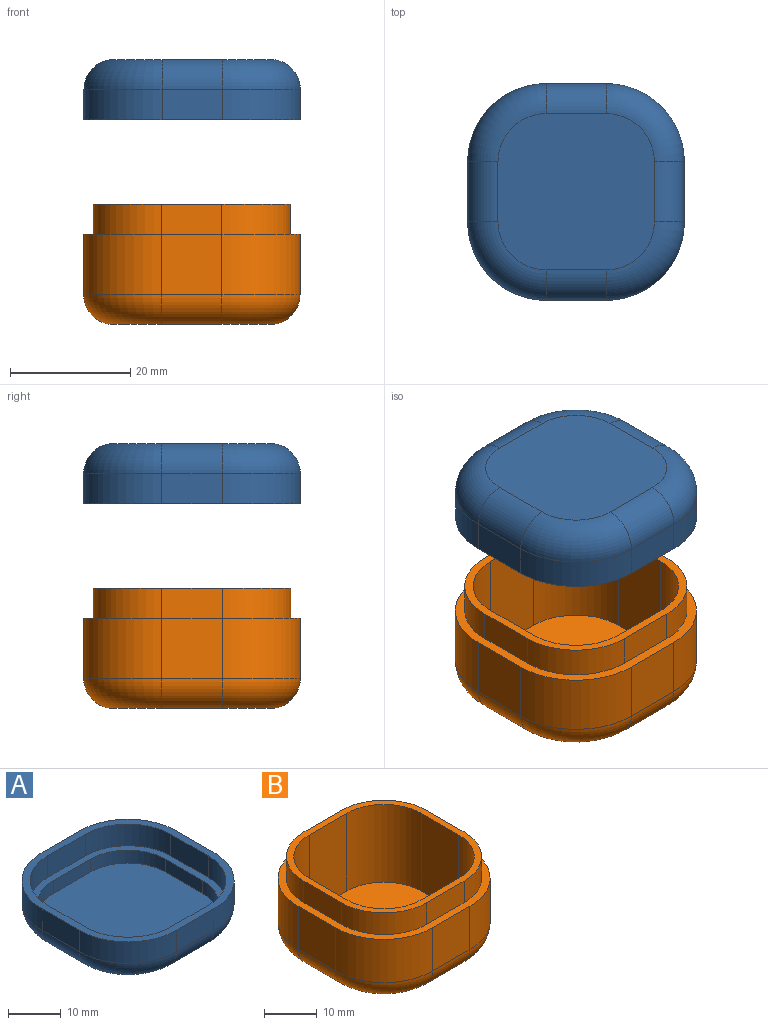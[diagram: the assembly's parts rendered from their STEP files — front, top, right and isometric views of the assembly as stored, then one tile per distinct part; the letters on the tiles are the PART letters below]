
ASSEMBLY  parts=2 mates=1
PART A: 36 faces, bbox 38.1x38.1x10 mm
  f0: plane 36x36mm, normal (0,0,1), area 181.1mm2, adj f2,f3,f4,f5,f6,f7,f8,f9
  f1: plane 26x26mm, normal (0,0,-1), area 621.1mm2, adj f28,f29,f30,f31,f32,f33,f34,f35
  f2: plane 10x5mm, normal (0,-1,0), area 50mm2, adj f0,f3,f9,f29
  f3: cylinder r=13mm len=13mm, axis (0,0,-1), area 102.1mm2, adj f0,f2,f4,f31
  f4: plane 10x5mm, normal (1,0,0), area 50mm2, adj f0,f3,f5,f33
  f5: cylinder r=13mm len=13mm, axis (0,0,-1), area 102.1mm2, adj f0,f4,f6,f35
  f6: plane 10x5mm, normal (0,1,0), area 50mm2, adj f0,f5,f7,f34
  f7: cylinder r=13mm len=13mm, axis (0,0,-1), area 102.1mm2, adj f0,f6,f8,f32
  f8: plane 10x5mm, normal (-1,0,0), area 50mm2, adj f0,f7,f9,f30
  f9: cylinder r=13mm len=13mm, axis (0,0,-1), area 102.1mm2, adj f0,f2,f8,f28
  f10: plane 10x5mm, normal (0,-1,0), area 50mm2, adj f0,f11,f17,f18
  f11: cylinder r=11.45mm len=11.45mm, axis (0,0,1), area 89.9mm2, adj f0,f10,f12,f18
  f12: plane 10x5mm, normal (1,0,0), area 50mm2, adj f0,f11,f13,f18
  f13: cylinder r=11.45mm len=11.45mm, axis (0,0,1), area 89.9mm2, adj f0,f12,f14,f18
  f14: plane 10x5mm, normal (0,1,0), area 50mm2, adj f0,f13,f15,f18
  f15: cylinder r=11.45mm len=11.45mm, axis (0,0,1), area 89.9mm2, adj f0,f14,f16,f18
  f16: plane 10x5mm, normal (-1,0,0), area 50mm2, adj f0,f15,f17,f18
  f17: cylinder r=11.45mm len=11.45mm, axis (0,0,1), area 89.9mm2, adj f0,f10,f16,f18
  f18: plane 32.9x32.9mm, normal (0,0,1), area 155.7mm2, adj f10,f11,f12,f13,f14,f15,f16,f17
  f19: plane 30x30mm, normal (0,0,1), area 814.2mm2, adj f20,f21,f22,f23,f24,f25,f26,f27
  f20: cylinder r=10mm len=10mm, axis (0,0,-1), area 47.1mm2, adj f18,f19,f22,f24
  f21: cylinder r=10mm len=10mm, axis (0,0,-1), area 47.1mm2, adj f18,f19,f22,f27
  f22: plane 10x3mm, normal (-1,0,0), area 30mm2, adj f18,f19,f20,f21
  f23: cylinder r=10mm len=10mm, axis (0,0,-1), area 47.1mm2, adj f18,f19,f24,f26
  f24: plane 10x3mm, normal (0,1,0), area 30mm2, adj f18,f19,f20,f23
  f25: cylinder r=10mm len=10mm, axis (0,0,-1), area 47.1mm2, adj f18,f19,f26,f27
  f26: plane 10x3mm, normal (1,0,0), area 30mm2, adj f18,f19,f23,f25
  f27: plane 10x3mm, normal (0,-1,0), area 30mm2, adj f18,f19,f21,f25
  f28: torus R=8mm, axis (0,0,1), area 138mm2, adj f1,f9,f29,f30
  f29: cylinder r=5mm len=10mm, axis (1,0,0), area 78.5mm2, adj f1,f2,f28,f31
  f30: cylinder r=5mm len=10mm, axis (0,-1,0), area 78.5mm2, adj f1,f8,f28,f32
  f31: torus R=8mm, axis (0,0,1), area 138mm2, adj f1,f3,f29,f33
  f32: torus R=8mm, axis (0,0,1), area 138mm2, adj f1,f7,f30,f34
  f33: cylinder r=5mm len=10mm, axis (0,1,0), area 78.5mm2, adj f1,f4,f31,f35
  f34: cylinder r=5mm len=10mm, axis (-1,0,0), area 78.5mm2, adj f1,f6,f32,f35
  f35: torus R=8mm, axis (0,0,1), area 138mm2, adj f1,f5,f33,f34
PART B: 36 faces, bbox 38.1x38.1x20 mm
  f0: plane 32.8x32.8mm, normal (0,0,1), area 150.1mm2, adj f1,f2,f3,f4,f5,f6,f7,f8
  f1: plane 18x10mm, normal (-1,0,0), area 180mm2, adj f0,f5,f6,f9
  f2: plane 18x10mm, normal (0,-1,0), area 180mm2, adj f0,f5,f8,f9
  f3: plane 18x10mm, normal (1,0,0), area 180mm2, adj f0,f7,f8,f9
  f4: plane 18x10mm, normal (0,1,0), area 180mm2, adj f0,f6,f7,f9
  f5: cylinder r=10mm len=18mm, axis (0,0,-1), area 282.7mm2, adj f0,f1,f2,f9
  f6: cylinder r=10mm len=18mm, axis (0,0,-1), area 282.7mm2, adj f0,f1,f4,f9
  f7: cylinder r=10mm len=18mm, axis (0,0,-1), area 282.7mm2, adj f0,f3,f4,f9
  f8: cylinder r=10mm len=18mm, axis (0,0,-1), area 282.7mm2, adj f0,f2,f3,f9
  f9: plane 30x30mm, normal (0,0,1), area 814.2mm2, adj f1,f2,f3,f4,f5,f6,f7,f8
  f10: cylinder r=11.4mm len=11.4mm, axis (0,0,1), area 89.5mm2, adj f0,f11,f17,f18
  f11: plane 10x5mm, normal (0,1,0), area 50mm2, adj f0,f10,f12,f18
  f12: cylinder r=11.4mm len=11.4mm, axis (0,0,1), area 89.5mm2, adj f0,f11,f13,f18
  f13: plane 10x5mm, normal (1,0,0), area 50mm2, adj f0,f12,f14,f18
  f14: cylinder r=11.4mm len=11.4mm, axis (0,0,1), area 89.5mm2, adj f0,f13,f15,f18
  f15: plane 10x5mm, normal (0,-1,0), area 50mm2, adj f0,f14,f16,f18
  f16: cylinder r=11.4mm len=11.4mm, axis (0,0,1), area 89.5mm2, adj f0,f15,f17,f18
  f17: plane 10x5mm, normal (-1,0,0), area 50mm2, adj f0,f10,f16,f18
  f18: plane 36x36mm, normal (0,0,1), area 186.6mm2, adj f10,f11,f12,f13,f14,f15,f16,f17
  f19: plane 26x26mm, normal (0,0,-1), area 621.1mm2, adj f28,f29,f30,f31,f32,f33,f34,f35
  f20: cylinder r=13mm len=13mm, axis (0,0,-1), area 204.2mm2, adj f18,f21,f27,f30
  f21: plane 10x10mm, normal (0,-1,0), area 100mm2, adj f18,f20,f22,f32
  f22: cylinder r=13mm len=13mm, axis (0,0,-1), area 204.2mm2, adj f18,f21,f23,f34
  f23: plane 10x10mm, normal (-1,0,0), area 100mm2, adj f18,f22,f24,f35
  f24: cylinder r=13mm len=13mm, axis (0,0,-1), area 204.2mm2, adj f18,f23,f25,f33
  f25: plane 10x10mm, normal (0,1,0), area 100mm2, adj f18,f24,f26,f31
  f26: cylinder r=13mm len=13mm, axis (0,0,-1), area 204.2mm2, adj f18,f25,f27,f29
  f27: plane 10x10mm, normal (1,0,0), area 100mm2, adj f18,f20,f26,f28
  f28: cylinder r=5mm len=10mm, axis (0,1,0), area 78.5mm2, adj f19,f27,f29,f30
  f29: torus R=8mm, axis (0,0,1), area 138mm2, adj f19,f26,f28,f31
  f30: torus R=8mm, axis (0,0,1), area 138mm2, adj f19,f20,f28,f32
  f31: cylinder r=5mm len=10mm, axis (-1,0,0), area 78.5mm2, adj f19,f25,f29,f33
  f32: cylinder r=5mm len=10mm, axis (1,0,0), area 78.5mm2, adj f19,f21,f30,f34
  f33: torus R=8mm, axis (0,0,1), area 138mm2, adj f19,f24,f31,f35
  f34: torus R=8mm, axis (0,0,1), area 138mm2, adj f19,f22,f32,f35
  f35: cylinder r=5mm len=10mm, axis (0,-1,0), area 78.5mm2, adj f19,f23,f33,f34
PLACE A rot(axis=(0,-1,0),180deg) t=(22.62,-36.5,56.73)mm
PLACE B rot(axis=(0.15,0.95,0.28),0deg) t=(22.57,-36.5,12.65)mm fixed
MATE slider B.f18 <-> A.f18  axis (0,0,1) through (6.17,-31.5,27.65)mm
